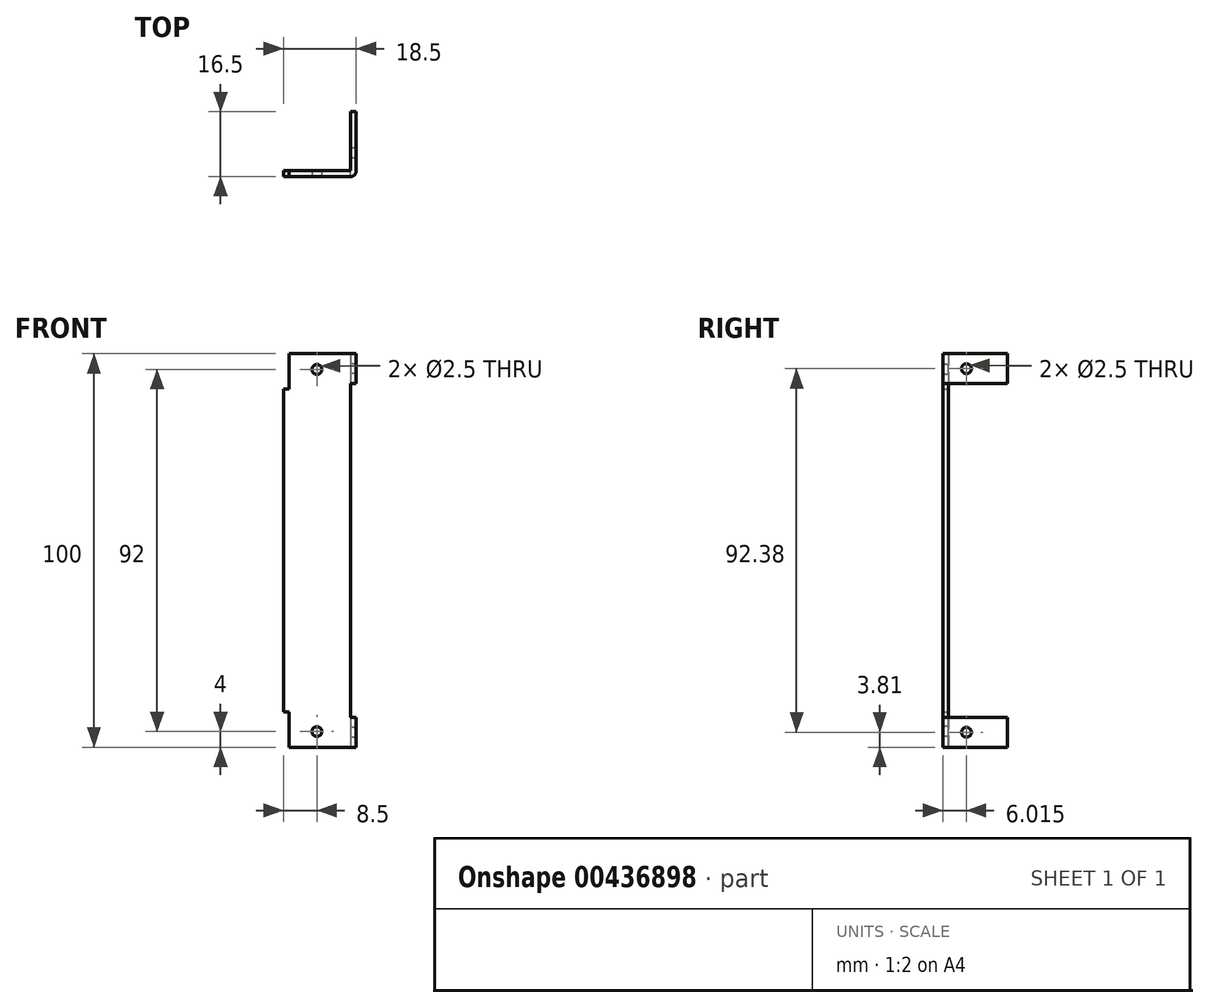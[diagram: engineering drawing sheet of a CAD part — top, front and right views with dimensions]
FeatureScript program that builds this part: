
annotation { "Feature Type Name" : "Feature", "Feature Type Description" : "" }
export const myFeature = defineFeature(function(context is Context, id is Id, definition is map)
    precondition{}
    {
        {
            var Q0;
            Q0=qCreatedBy(makeId("Front.planeOp"),FACE);
            var sketch = newSketch(context, id + "F0", { "sketchPlane" : qUnion([Q0])});
            skLineSegment(sketch, "E0.bottom", {"start": v(0, 0) * mm, "end": v(17, 0) * mm});
            skLineSegment(sketch, "E0.top", {"start": v(0, 100) * mm, "end": v(17, 100) * mm});
            skLineSegment(sketch, "E0.left", {"start": v(0, 0) * mm, "end": v(0, 100) * mm});
            skLineSegment(sketch, "E0.right", {"start": v(17, 0) * mm, "end": v(17, 100) * mm});
            skSolve(sketch);
        }
        {
            var Q0;
            Q0 = qSketchRegion(id + "F0", true);
            extrude(context, id + "F1", {"entities" : qUnion([Q0]), "depth" : 1.5 * mm});
        }
        {
            var Q0;
            Q0=makeQuery(id+"F1.opExtrude","CAP_FACE",FACE,{"disambiguationData":[OSD([sQuery(id+"F0.wireOp",EDGE,"E0.bottom"),sQuery(id+"F0.wireOp",EDGE,"E0.top"),sQuery(id+"F0.wireOp",EDGE,"E0.left"),sQuery(id+"F0.wireOp",EDGE,"E0.right")])],"isStart":false});
            var sketch = newSketch(context, id + "F2", { "sketchPlane" : qUnion([Q0])});
            skPoint(sketch, "E1", {"position": v(8.5, 4) * mm});
            skPoint(sketch, "E2", {"position": v(8.5, 96) * mm});
            skSolve(sketch);
        }
        {
            var Q0;
            Q0=sQuery(id+"F2.wireOp",VERTEX,"E2");
            var Q1;
            Q1=sQuery(id+"F2.wireOp",VERTEX,"E1");
            var Q2;
            Q2=makeQuery(id+"F1.opExtrude","SWEPT_BODY",BODY,{"disambiguationData":[OSD([sQuery(id+"F0.wireOp",EDGE,"E0.bottom"),sQuery(id+"F0.wireOp",EDGE,"E0.top"),sQuery(id+"F0.wireOp",EDGE,"E0.left"),sQuery(id+"F0.wireOp",EDGE,"E0.right")])]});
            hole(context, id + "F3", {"style" : HoleStyle.SIMPLE, "endStyle" : HoleEndStyle.THROUGH, "standardTappedOrClearance" : lookupTablePath({ "standard" : "ISO", "engagement" : "75%", "pitch" : "0.5 mm", "size" : "M3", "type" : "Tapped" }), "standardBlindInLast" : lookupTablePath({ "standard" : "ISO", "engagement" : "75%", "pitch" : "0.5 mm", "size" : "M3", "type" : "Tapped" }), "holeDiameter" : 2.5 * mm, "showTappedDepth" : true, "isTappedThrough" : true, "tappedDepth" : 12 * mm, "tapClearance" : 3, "locations" : qUnion([Q0, Q1]), "scope" : qUnion([Q2]), "majorDiameter" : 3 * mm});
        }
        {
            var Q0;
            Q0=makeQuery(id+"F1.opExtrude","SWEPT_FACE",FACE,{"disambiguationData":[OSD([sQuery(id+"F0.wireOp",EDGE,"E0.right")])]});
            var sketch = newSketch(context, id + "F4", { "sketchPlane" : qUnion([Q0])});
            skLineSegment(sketch, "E3.bottom", {"start": v(-1.5, 100) * mm, "end": v(0, 100) * mm});
            skLineSegment(sketch, "E3.top", {"start": v(-1.5, 92.38) * mm, "end": v(0, 92.38) * mm});
            skLineSegment(sketch, "E3.left", {"start": v(-1.5, 100) * mm, "end": v(-1.5, 92.38) * mm});
            skLineSegment(sketch, "E3.right", {"start": v(0, 100) * mm, "end": v(0, 92.38) * mm});
            skLineSegment(sketch, "E4.bottom", {"start": v(-1.5, 7.62) * mm, "end": v(0, 7.62) * mm});
            skLineSegment(sketch, "E4.top", {"start": v(-1.5, 0) * mm, "end": v(0, 0) * mm});
            skLineSegment(sketch, "E4.left", {"start": v(-1.5, 7.62) * mm, "end": v(-1.5, 0) * mm});
            skLineSegment(sketch, "E4.right", {"start": v(0, 7.62) * mm, "end": v(0, 0) * mm});
            skLineSegment(sketch, "E5", {"start": v(-1.5, 50) * mm, "end": v(0, 50) * mm});
            skSolve(sketch);
        }
        {
            var Q0;
            Q0 = qSketchRegion(id + "F4", true);
            var Q1;
            Q1=makeQuery(id+"F1.opExtrude","CAP_EDGE",EDGE,{"disambiguationData":[OSD([sQuery(id+"F0.wireOp",EDGE,"E0.right")])],"isStart":true});
            revolve(context, id + "F5", {"operationType" : NewBodyOperationType.ADD, "entities" : qUnion([Q0]), "axis" : qUnion([Q1]), "revolveType" : RevolveType.ONE_DIRECTION, "angle" : 90 * degree});
        }
        {
            var Q0;
            Q0=makeQuery(id+"F5.boolean.opBoolean","MERGE",FACE,{"derivedFrom":[makeQuery(id+"F1.opExtrude","CAP_FACE",FACE,{"disambiguationData":[OSD([sQuery(id+"F0.wireOp",EDGE,"E0.bottom"),sQuery(id+"F0.wireOp",EDGE,"E0.top"),sQuery(id+"F0.wireOp",EDGE,"E0.left"),sQuery(id+"F0.wireOp",EDGE,"E0.right")])],"isStart":true}),makeQuery(id+"F5.opRevolve","CAP_FACE",FACE,{"disambiguationData":[OSD([sQuery(id+"F4.wireOp",EDGE,"E3.bottom"),sQuery(id+"F4.wireOp",EDGE,"E3.top"),sQuery(id+"F4.wireOp",EDGE,"E3.left"),sQuery(id+"F4.wireOp",EDGE,"E3.right")])],"isStart":false}),makeQuery(id+"F5.opRevolve","CAP_FACE",FACE,{"disambiguationData":[OSD([sQuery(id+"F4.wireOp",EDGE,"E4.bottom"),sQuery(id+"F4.wireOp",EDGE,"E4.top"),sQuery(id+"F4.wireOp",EDGE,"E4.left"),sQuery(id+"F4.wireOp",EDGE,"E4.right")])],"isStart":false})]});
            var sketch = newSketch(context, id + "F6", { "sketchPlane" : qUnion([Q0])});
            skLineSegment(sketch, "E6.bottom", {"start": v(-18.5, 7.62) * mm, "end": v(-17, 7.62) * mm});
            skLineSegment(sketch, "E6.top", {"start": v(-18.5, 0) * mm, "end": v(-17, 0) * mm});
            skLineSegment(sketch, "E6.left", {"start": v(-18.5, 7.62) * mm, "end": v(-18.5, 0) * mm});
            skLineSegment(sketch, "E6.right", {"start": v(-17, 7.62) * mm, "end": v(-17, 0) * mm});
            skLineSegment(sketch, "E7.bottom", {"start": v(-18.5, 100) * mm, "end": v(-17, 100) * mm});
            skLineSegment(sketch, "E7.top", {"start": v(-18.5, 92.38) * mm, "end": v(-17, 92.38) * mm});
            skLineSegment(sketch, "E7.left", {"start": v(-18.5, 100) * mm, "end": v(-18.5, 92.38) * mm});
            skLineSegment(sketch, "E7.right", {"start": v(-17, 100) * mm, "end": v(-17, 92.38) * mm});
            skSolve(sketch);
        }
        {
            var Q0;
            Q0 = qSketchRegion(id + "F6", true);
            extrude(context, id + "F7", {"entities" : qUnion([Q0]), "operationType" : NewBodyOperationType.ADD, "depth" : 15 * mm});
        }
        {
            var Q0;
            Q0=makeQuery(id+"F7.opExtrude","SWEPT_FACE",FACE,{"disambiguationData":[OSD([sQuery(id+"F6.wireOp",EDGE,"E7.right")])]});
            var sketch = newSketch(context, id + "F8", { "sketchPlane" : qUnion([Q0])});
            skPoint(sketch, "E8", {"position": v(-4.51, 96.19) * mm});
            skPoint(sketch, "E8.positionSnap0", {"position": v(-15, 96.19) * mm});
            skPoint(sketch, "E9", {"position": v(-4.51, 3.81) * mm});
            skSolve(sketch);
        }
        {
            var Q0;
            Q0=sQuery(id+"F8.wireOp",VERTEX,"E8");
            var Q1;
            Q1=sQuery(id+"F8.wireOp",VERTEX,"E9");
            var Q2;
            Q2=makeQuery(id+"F1.opExtrude","SWEPT_BODY",BODY,{"disambiguationData":[OSD([sQuery(id+"F0.wireOp",EDGE,"E0.bottom"),sQuery(id+"F0.wireOp",EDGE,"E0.top"),sQuery(id+"F0.wireOp",EDGE,"E0.left"),sQuery(id+"F0.wireOp",EDGE,"E0.right")])]});
            hole(context, id + "F9", {"style" : HoleStyle.SIMPLE, "endStyle" : HoleEndStyle.THROUGH, "standardTappedOrClearance" : lookupTablePath({ "standard" : "ISO", "engagement" : "75%", "pitch" : "0.5 mm", "size" : "M3", "type" : "Tapped" }), "standardBlindInLast" : lookupTablePath({ "standard" : "ISO", "engagement" : "75%", "pitch" : "0.5 mm", "size" : "M3", "type" : "Tapped" }), "holeDiameter" : 2.5 * mm, "showTappedDepth" : true, "isTappedThrough" : true, "tappedDepth" : 12 * mm, "tapClearance" : 3, "locations" : qUnion([Q0, Q1]), "scope" : qUnion([Q2]), "majorDiameter" : 3 * mm});
        }
        {
            var Q0;
            Q0=makeQuery(id+"F5.boolean.opBoolean","MERGE",FACE,{"derivedFrom":[makeQuery(id+"F1.opExtrude","CAP_FACE",FACE,{"disambiguationData":[OSD([sQuery(id+"F0.wireOp",EDGE,"E0.bottom"),sQuery(id+"F0.wireOp",EDGE,"E0.top"),sQuery(id+"F0.wireOp",EDGE,"E0.left"),sQuery(id+"F0.wireOp",EDGE,"E0.right")])],"isStart":true}),makeQuery(id+"F5.opRevolve","CAP_FACE",FACE,{"disambiguationData":[OSD([sQuery(id+"F4.wireOp",EDGE,"E3.bottom"),sQuery(id+"F4.wireOp",EDGE,"E3.top"),sQuery(id+"F4.wireOp",EDGE,"E3.left"),sQuery(id+"F4.wireOp",EDGE,"E3.right")])],"isStart":false}),makeQuery(id+"F5.opRevolve","CAP_FACE",FACE,{"disambiguationData":[OSD([sQuery(id+"F4.wireOp",EDGE,"E4.bottom"),sQuery(id+"F4.wireOp",EDGE,"E4.top"),sQuery(id+"F4.wireOp",EDGE,"E4.left"),sQuery(id+"F4.wireOp",EDGE,"E4.right")])],"isStart":false})]});
            var sketch = newSketch(context, id + "F10", { "sketchPlane" : qUnion([Q0])});
            skLineSegment(sketch, "E10.bottom", {"start": v(0, 100) * mm, "end": v(-1.5, 100) * mm});
            skLineSegment(sketch, "E10.top", {"start": v(0, 91) * mm, "end": v(-1.5, 91) * mm});
            skLineSegment(sketch, "E10.left", {"start": v(0, 100) * mm, "end": v(0, 91) * mm});
            skLineSegment(sketch, "E10.right", {"start": v(-1.5, 100) * mm, "end": v(-1.5, 91) * mm});
            skLineSegment(sketch, "E11.bottom", {"start": v(0, 0) * mm, "end": v(-1.5, 0) * mm});
            skLineSegment(sketch, "E11.top", {"start": v(0, 9) * mm, "end": v(-1.5, 9) * mm});
            skLineSegment(sketch, "E11.left", {"start": v(0, 0) * mm, "end": v(0, 9) * mm});
            skLineSegment(sketch, "E11.right", {"start": v(-1.5, 0) * mm, "end": v(-1.5, 9) * mm});
            skSolve(sketch);
        }
        {
            var Q0;
            Q0 = qSketchRegion(id + "F10", true);
            extrude(context, id + "F11", {"entities" : qUnion([Q0]), "operationType" : NewBodyOperationType.REMOVE, "endBound" : BoundingType.THROUGH_ALL, "oppositeDirection" : true, "depth" : 25 * mm, "offsetDistance" : 25 * mm});
        }
    });
